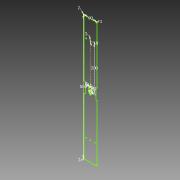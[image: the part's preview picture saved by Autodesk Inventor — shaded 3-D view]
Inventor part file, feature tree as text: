
AUTODESK INVENTOR PART (.ipt)
format: ipt  version: 2015 (Build 190159000, 159)  size: 92,160 bytes
history: native  units: mm
features: sketch x1
ambient origin geometry x8: Origin, YZ Plane, XZ Plane, XY Plane, X Axis, Y Axis, Z Axis, Center Point
feature tree (1):
  sketch  "Sketch1"  dims[d0=60.0mm d1=580.0mm d5=5.0mm d6=10.0mm d7=3.0mm d8=1.0mm d9=1.0mm d10=1.0mm d11=1.0mm d12=4.0mm d13=3.0mm d16=200.0mm d17=3.0mm d18=10.0mm d19=2.0mm d20=2.0mm d21=2.0mm]
